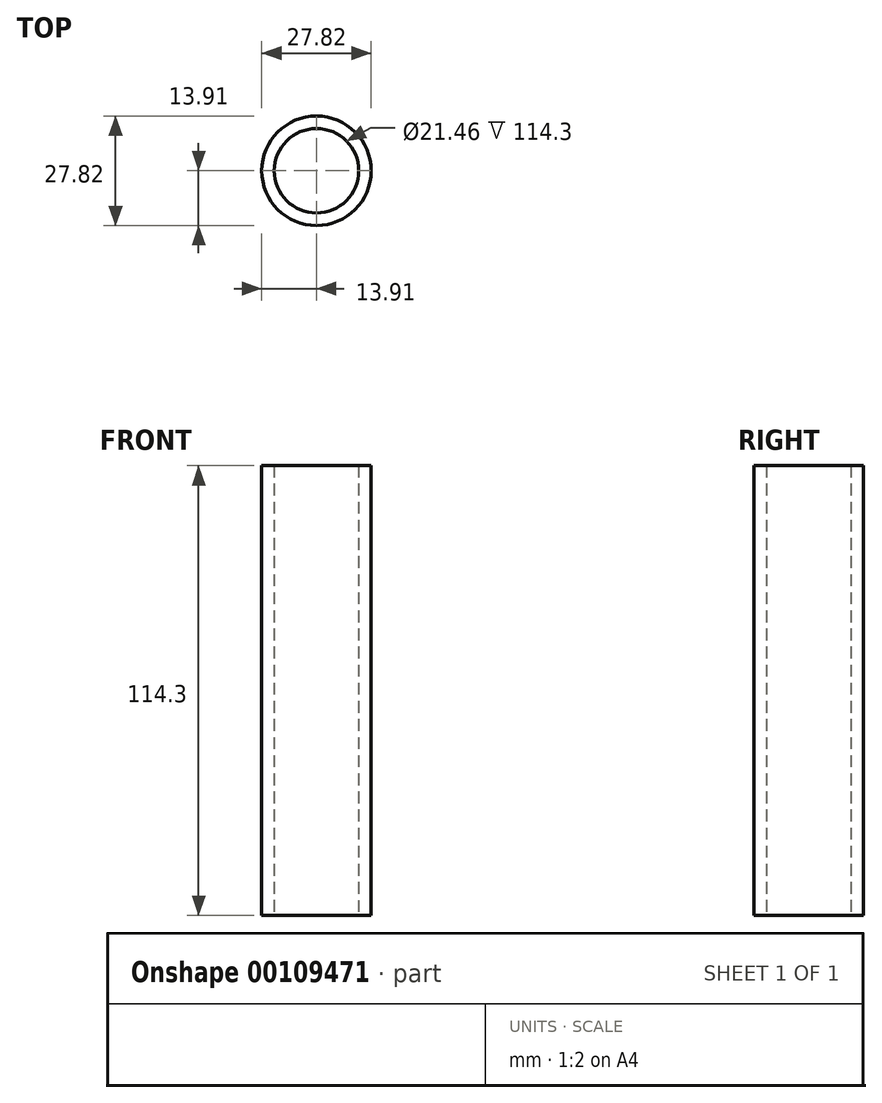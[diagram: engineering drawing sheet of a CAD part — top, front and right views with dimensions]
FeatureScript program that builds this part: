
annotation { "Feature Type Name" : "Feature", "Feature Type Description" : "" }
export const myFeature = defineFeature(function(context is Context, id is Id, definition is map)
    precondition{}
    {
        {
            var Q0;
            Q0=qCreatedBy(makeId("Top.planeOp"),FACE);
            var sketch = newSketch(context, id + "F0", { "sketchPlane" : qUnion([Q0])});
            skCircle(sketch, "E0", {"center": v(0, 0) * mm, "radius": 10.73 * mm});
            skCircle(sketch, "E1", {"center": v(0, 0) * mm, "radius": 13.9 * mm});
            skSolve(sketch);
        }
        {
            var Q0;
            Q0=makeQuery(id+"F0.imprint","IMPRINT",FACE,{"disambiguationData":[TD([[makeQuery(id+"F0.imprint","IMPRINT",EDGE,{"derivedFrom":sQuery(id+"F0.wireOp",EDGE,"E0")}),-1.0]])]});
            extrude(context, id + "F1", {"entities" : qUnion([Q0]), "depth" : 114.3 * mm});
        }
    });
